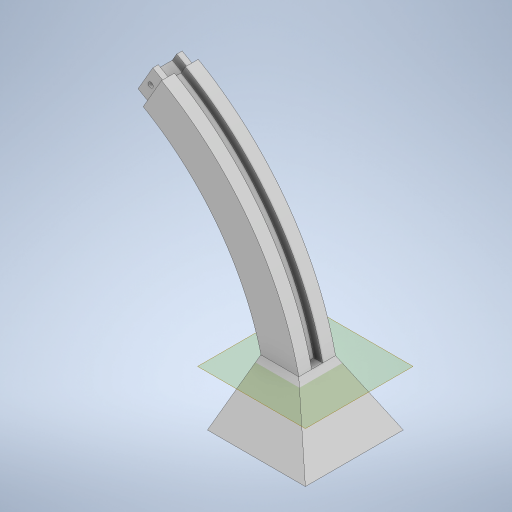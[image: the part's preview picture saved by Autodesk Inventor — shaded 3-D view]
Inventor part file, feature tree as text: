
AUTODESK INVENTOR PART (.ipt)
format: ipt  version: 2023 (Build 270158000, 158)  size: 367,104 bytes
history: native  units: mm
features: sketch x9, extrude x3, plane x3, loft x2, sweep x1
ambient origin geometry x8: Origin, YZ Plane, XZ Plane, XY Plane, X Axis, Y Axis, Z Axis, Center Point
bodies: Body1 (feature_tree)
feature tree (18):
  sweep  "Sweep2"
  extrude  "Extrusion3"  Depth=7.0mm
  extrude  "Extrusion4"  Depth=15.0mm
  sketch  "Sketch9"  dims[d41=220.0mm d42=60.0deg]
  plane  "Work Plane1"
  loft  "Loft1"
  plane  "Work Plane2"
  extrude  "Extrusion5"  TaperAngle=60.0deg  [1 undecoded]
  sketch  "Sketch12"  dims[d47=3.0mm]
  plane  "Work Plane3"
  loft  "Loft2"
  sketch  "Sketch2"  dims[d5=100.0mm d18=9.0mm]
  sketch  "Sketch6"  dims[d19=7.0mm d21=16.0mm]
  sketch  "Sketch7"  dims[d22=30.0mm d23=15.0mm]
  sketch  "Sketch8"  dims[d24=4.5mm d25=8.0mm]
  sketch  "Sketch10"  dims[d43=220.0mm d44=0.0mm]
  sketch  "Sketch11"  dims[d45=0.0mm d46=0.0mm]
  sketch  "Sketch14"  dims[d48=3.0mm d49=3.0mm d50=3.0mm d51=3.0mm d52=3.0mm d53=3.0mm d54=3.0mm d55=3.0mm d56=10.0mm d57=0.0mm d58=4.0mm d59=12.0mm d60=5.0mm d61=0.0mm d62=0.0mm d63=80.0mm d64=80.0mm d65=40.0mm d66=40.0mm d67=50.0mm d68=30.0mm d69=9.6mm d70=15.0mm d71=31.0mm d72=0.0mm d73=90.0deg d74=0.0mm d75=90.0deg d76=-79.0mm d77=100.0mm d79=140.0mm d80=67.608902mm d81=140.0mm d82=150.0deg d83=50.0mm d84=0.0mm d85=0.0mm d86=5.0mm d87=10.0mm d88=10.0mm d89=10.0mm d90=10.0mm d91=-45.0mm d95=1.0mm d96=1.0mm d97=39.5mm d98=39.5mm d99=0.0mm d100=90.0deg d101=0.0mm d102=90.0deg]
note: 1 required parameter value undecoded (feature->parameter linkage not recoverable at this tier; creation-order binding heuristic only, values carry confidence <= 0.55)
